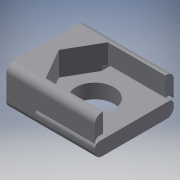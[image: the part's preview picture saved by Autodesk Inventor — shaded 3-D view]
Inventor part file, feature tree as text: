
AUTODESK INVENTOR PART (.ipt)
format: ipt  version: 2016 (Build 200138000, 138)  size: 152,576 bytes
history: native  units: in
note: dims shown in document units (in); Inventor stores cm internally (conversion verified against a paired STEP export)
features: sketch x7, other x3
ambient origin geometry x8: Origin, YZ Plane, XZ Plane, XY Plane, X Axis, Y Axis, Z Axis, Center Point
bodies: Solid1 (feature_tree)
feature tree (10):
  other  "nut holder.ipt"
  other  "Solid1::nut holder.ipt"
  other  "TaggingFeature1"
  sketch  "Sketch1"  dims[d0=0.3937in]
  sketch  "Sketch2"
  sketch  "Sketch3"
  sketch  "Sketch4"
  sketch  "Sketch5"
  sketch  "Sketch6"
  sketch  "Sketch7"
